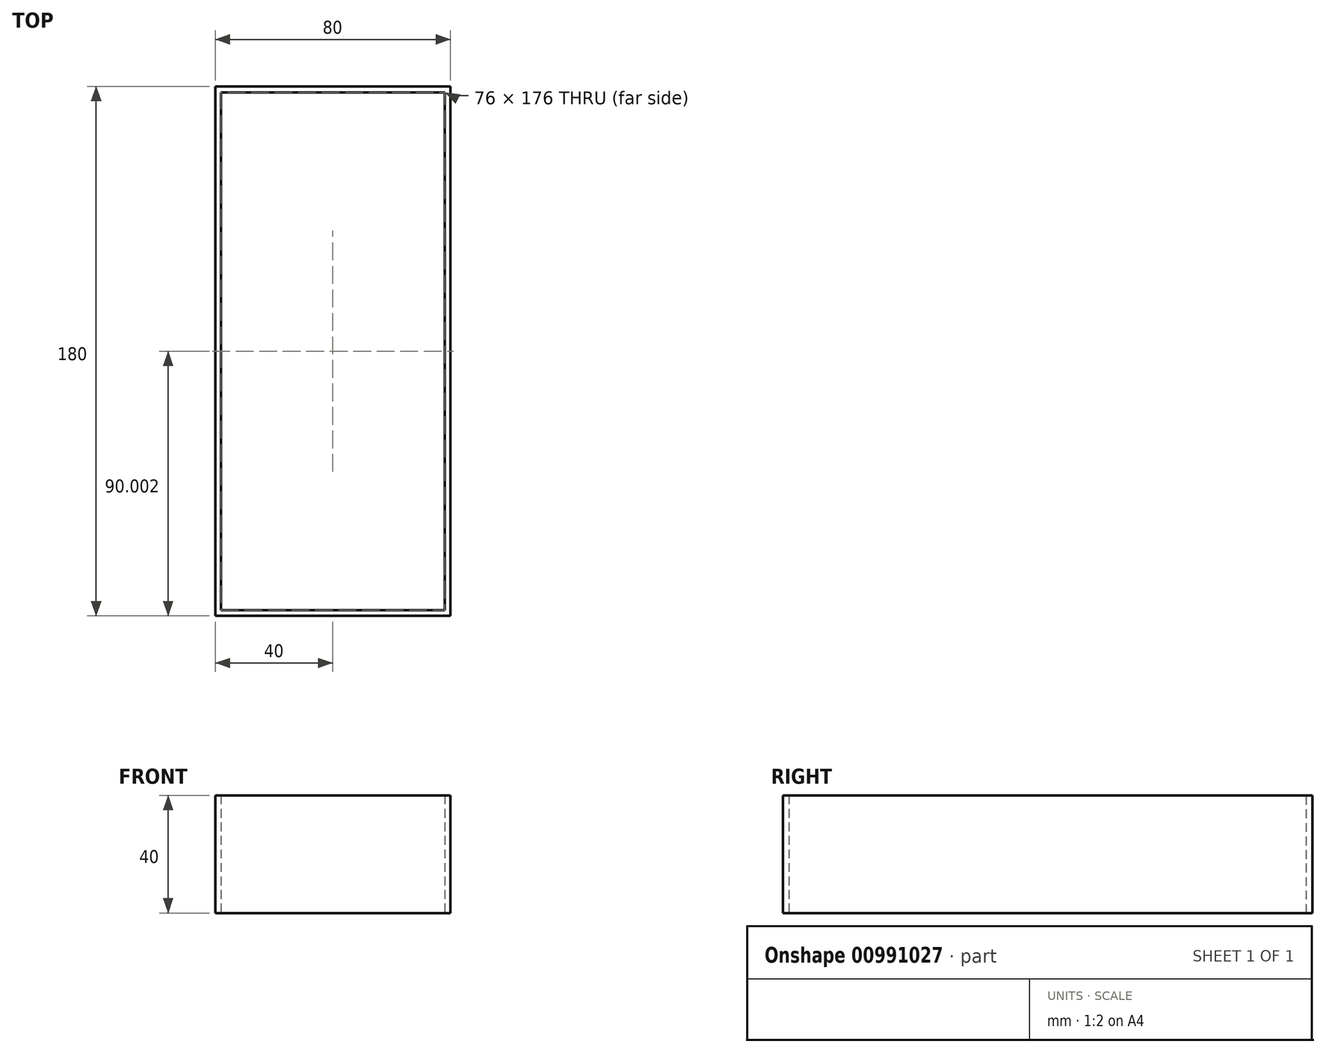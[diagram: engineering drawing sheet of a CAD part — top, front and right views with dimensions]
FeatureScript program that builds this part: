
annotation { "Feature Type Name" : "Feature", "Feature Type Description" : "" }
export const myFeature = defineFeature(function(context is Context, id is Id, definition is map)
    precondition{}
    {
        {
            var Q0;
            Q0=qCreatedBy(makeId("Right.planeOp"),FACE);
            var sketch = newSketch(context, id + "F0", { "sketchPlane" : qUnion([Q0])});
            skLineSegment(sketch, "E0", {"start": v(-80.99, -43.53) * mm, "end": v(99.01, -43.53) * mm});
            skLineSegment(sketch, "E1", {"start": v(99.01, -43.53) * mm, "end": v(99.01, -3.53) * mm});
            skLineSegment(sketch, "E2", {"start": v(99.01, -3.53) * mm, "end": v(-80.99, -3.53) * mm});
            skLineSegment(sketch, "E3", {"start": v(-80.99, -3.53) * mm, "end": v(-80.99, -43.53) * mm});
            skSolve(sketch);
        }
        {
            var Q0;
            Q0 = qSketchRegion(id + "F0", true);
            extrude(context, id + "F1", {"entities" : qUnion([Q0]), "endBound" : BoundingType.SYMMETRIC, "depth" : 80 * mm, "offsetDistance" : 25 * mm});
        }
        {
            var Q0;
            Q0=makeQuery(id+"F1.opExtrude","SWEPT_FACE",FACE,{"disambiguationData":[OSD([sQuery(id+"F0.wireOp",EDGE,"E2")])]});
            var Q1;
            Q1=makeQuery(id+"F1.opExtrude","SWEPT_FACE",FACE,{"disambiguationData":[OSD([sQuery(id+"F0.wireOp",EDGE,"E0")])]});
            shell(context, id + "F2", {"entities" : qUnion([Q0, Q1]), "thickness" : 2 * mm});
        }
    });
